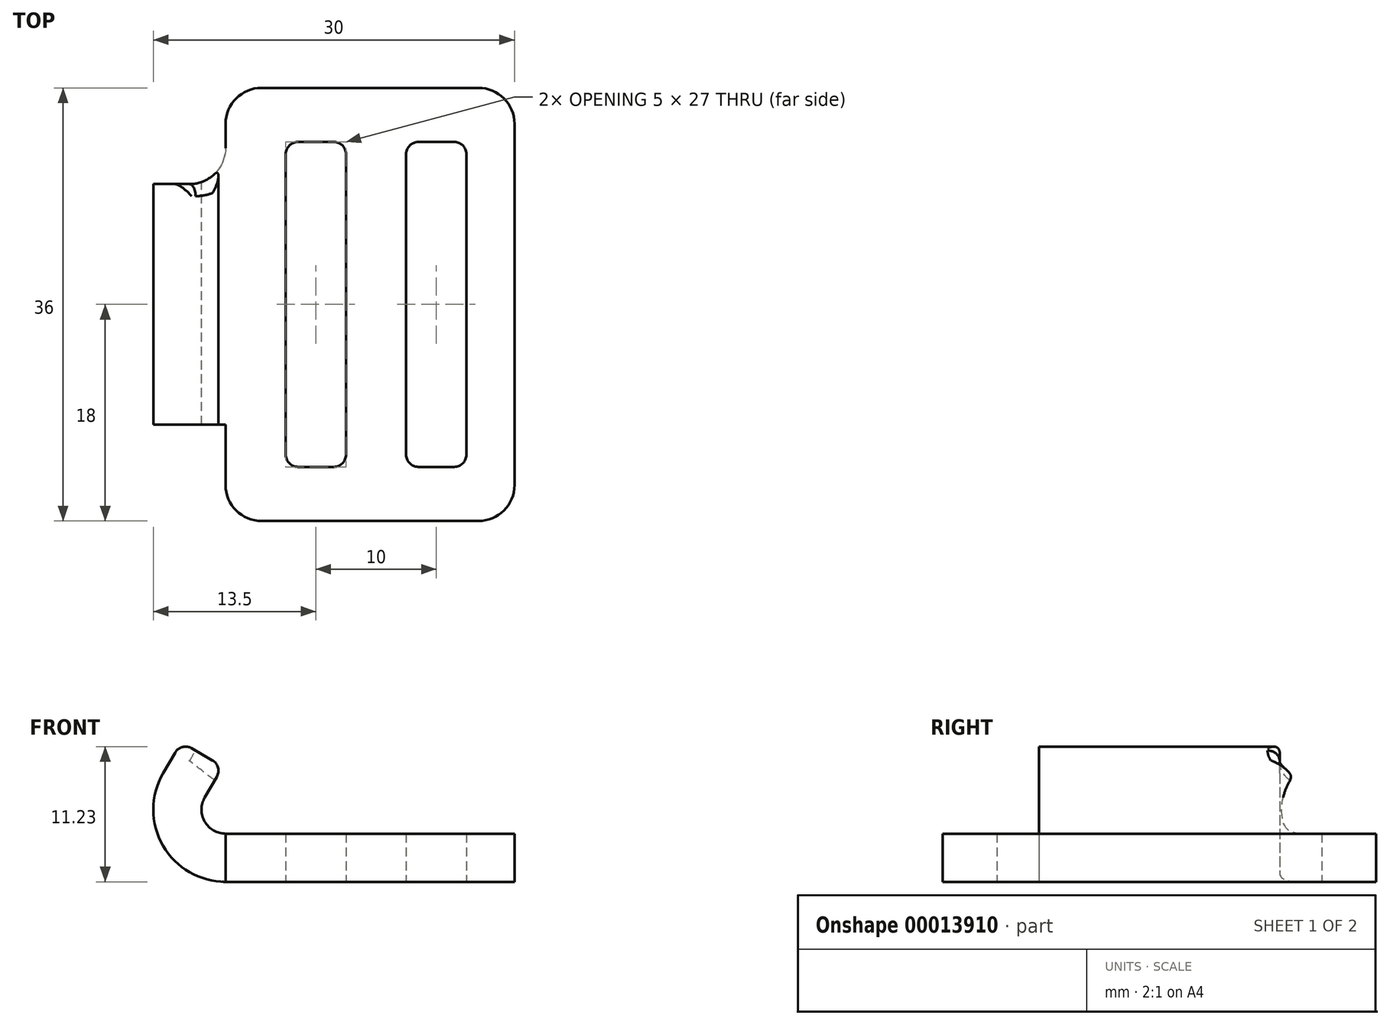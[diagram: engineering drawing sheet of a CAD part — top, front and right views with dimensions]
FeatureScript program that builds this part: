
annotation { "Feature Type Name" : "Feature", "Feature Type Description" : "" }
export const myFeature = defineFeature(function(context is Context, id is Id, definition is map)
    precondition{}
    {
        {
            var Q0;
            Q0=qCreatedBy(makeId("Top.planeOp"),FACE);
            var sketch = newSketch(context, id + "F0", { "sketchPlane" : qUnion([Q0])});
            skLineSegment(sketch, "E0.bottom", {"start": v(13, 18) * mm, "end": v(31, 18) * mm});
            skLineSegment(sketch, "E0.top", {"start": v(13, -18) * mm, "end": v(31, -18) * mm});
            skLineSegment(sketch, "E0.left", {"start": v(10, 15) * mm, "end": v(10, -13.27) * mm});
            skLineSegment(sketch, "E0.right", {"start": v(34, 15) * mm, "end": v(34, -15) * mm});
            skLineSegment(sketch, "E1.trimOffspring", {"start": v(10, -13.27) * mm, "end": v(10, -15) * mm});
            skLineSegment(sketch, "E2.bottom", {"start": v(16, 13.5) * mm, "end": v(19, 13.5) * mm});
            skLineSegment(sketch, "E2.top", {"start": v(16, -13.5) * mm, "end": v(19, -13.5) * mm});
            skLineSegment(sketch, "E2.left", {"start": v(15, 12.5) * mm, "end": v(15, -12.5) * mm});
            skLineSegment(sketch, "E2.right", {"start": v(20, 12.5) * mm, "end": v(20, -12.5) * mm});
            skLineSegment(sketch, "E3.bottom", {"start": v(26, 13.5) * mm, "end": v(29, 13.5) * mm});
            skLineSegment(sketch, "E3.top", {"start": v(26, -13.5) * mm, "end": v(29, -13.5) * mm});
            skLineSegment(sketch, "E3.left", {"start": v(25, 12.5) * mm, "end": v(25, -12.5) * mm});
            skLineSegment(sketch, "E3.right", {"start": v(30, 12.5) * mm, "end": v(30, -12.5) * mm});
            skLineSegment(sketch, "E4", {"start": v(0, 0) * mm, "end": v(34, 0) * mm, "construction": true});
            skPoint(sketch, "E5", {"position": v(25, 0) * mm});
            skPoint(sketch, "E6.visualSharp", {"position": v(10, -18) * mm});
            skArc(sketch, "E6.filletArc", {"start": v(10, -15) * mm, "mid": v(10.88, -17.12) * mm, "end": v(13, -18) * mm});
            skPoint(sketch, "E7.visualSharp", {"position": v(34, -18) * mm});
            skArc(sketch, "E7.filletArc", {"start": v(31, -18) * mm, "mid": v(33.12, -17.12) * mm, "end": v(34, -15) * mm});
            skPoint(sketch, "E8.visualSharp", {"position": v(34, 18) * mm});
            skArc(sketch, "E8.filletArc", {"start": v(34, 15) * mm, "mid": v(33.12, 17.12) * mm, "end": v(31, 18) * mm});
            skPoint(sketch, "E9.visualSharp", {"position": v(10, 18) * mm});
            skArc(sketch, "E9.filletArc", {"start": v(13, 18) * mm, "mid": v(10.88, 17.12) * mm, "end": v(10, 15) * mm});
            skPoint(sketch, "E10.visualSharp", {"position": v(15, 13.5) * mm});
            skArc(sketch, "E10.filletArc", {"start": v(16, 13.5) * mm, "mid": v(15.3, 13.2) * mm, "end": v(15, 12.5) * mm});
            skPoint(sketch, "E11.visualSharp", {"position": v(20, 13.5) * mm});
            skArc(sketch, "E11.filletArc", {"start": v(20, 12.5) * mm, "mid": v(19.7, 13.2) * mm, "end": v(19, 13.5) * mm});
            skPoint(sketch, "E12.visualSharp", {"position": v(25, 13.5) * mm});
            skArc(sketch, "E12.filletArc", {"start": v(26, 13.5) * mm, "mid": v(25.3, 13.2) * mm, "end": v(25, 12.5) * mm});
            skPoint(sketch, "E13.visualSharp", {"position": v(30, 13.5) * mm});
            skArc(sketch, "E13.filletArc", {"start": v(30, 12.5) * mm, "mid": v(29.7, 13.2) * mm, "end": v(29, 13.5) * mm});
            skPoint(sketch, "E14.visualSharp", {"position": v(30, -13.5) * mm});
            skArc(sketch, "E14.filletArc", {"start": v(29, -13.5) * mm, "mid": v(29.7, -13.2) * mm, "end": v(30, -12.5) * mm});
            skPoint(sketch, "E15.visualSharp", {"position": v(25, -13.5) * mm});
            skArc(sketch, "E15.filletArc", {"start": v(25, -12.5) * mm, "mid": v(25.3, -13.2) * mm, "end": v(26, -13.5) * mm});
            skPoint(sketch, "E16.visualSharp", {"position": v(15, -13.5) * mm});
            skArc(sketch, "E16.filletArc", {"start": v(15, -12.5) * mm, "mid": v(15.3, -13.2) * mm, "end": v(16, -13.5) * mm});
            skPoint(sketch, "E17.visualSharp", {"position": v(20, -13.5) * mm});
            skArc(sketch, "E17.filletArc", {"start": v(19, -13.5) * mm, "mid": v(19.7, -13.2) * mm, "end": v(20, -12.5) * mm});
            skSolve(sketch);
        }
        {
            var Q0;
            Q0=qSketchRegion(id+"F0",true);
            extrude(context, id + "F1", {"entities" : qUnion([Q0]), "depth" : 4 * mm});
        }
        {
            var Q0;
            Q0=qCreatedBy(makeId("Front.planeOp"),FACE);
            var sketch = newSketch(context, id + "F2", { "sketchPlane" : qUnion([Q0])});
            skArc(sketch, "E18", {"start": v(4.8, 9) * mm, "mid": v(4.8, 3) * mm, "end": v(10, 0) * mm});
            skLineSegment(sketch, "E19", {"start": v(10, 0) * mm, "end": v(13, 0) * mm, "construction": true});
            skArc(sketch, "E20", {"start": v(8.27, 7) * mm, "mid": v(8.27, 5) * mm, "end": v(10, 4) * mm});
            skLineSegment(sketch, "E21", {"start": v(10, 6) * mm, "end": v(4.8, 9) * mm, "construction": true});
            skLineSegment(sketch, "E22", {"start": v(4.8, 9) * mm, "end": v(6.3, 11.6) * mm});
            skLineSegment(sketch, "E23", {"start": v(6.3, 11.6) * mm, "end": v(9.77, 9.6) * mm});
            skLineSegment(sketch, "E24", {"start": v(9.77, 9.6) * mm, "end": v(8.27, 7) * mm});
            skLineSegment(sketch, "E25", {"start": v(10, 4) * mm, "end": v(10, 0) * mm});
            skSolve(sketch);
        }
        {
            var Q0;
            Q0 = qSketchRegion(id + "F2", true);
            extrude(context, id + "F3", {"entities" : qUnion([Q0]), "operationType" : NewBodyOperationType.ADD, "depth" : 10 * mm, "hasSecondDirection" : true, "secondDirectionOppositeDirection" : true, "secondDirectionDepth" : 10 * mm});
        }
        {
            var Q0;
            Q0=makeQuery(id+"F3.opExtrude","CAP_EDGE",EDGE,{"disambiguationData":[OSD([sQuery(id+"F2.wireOp",EDGE,"E25")])],"isStart":false});
            var Q1;
            Q1=makeQuery(id+"F3.opExtrude","CAP_EDGE",EDGE,{"disambiguationData":[OSD([sQuery(id+"F2.wireOp",EDGE,"E25")])],"isStart":true});
            fillet(context, id + "F4", {"entities" : qUnion([Q0, Q1]), "radius" : 3 * mm, "tangentPropagation" : true, "allowEdgeOverflow" : false});
        }
        {
            var Q0;
            Q0=makeQuery(id+"F4.opFillet","BLEND_EDGE",EDGE,{"blendedFrom":[makeQuery(id+"F3.opExtrude","CAP_EDGE",EDGE,{"disambiguationData":[OSD([sQuery(id+"F2.wireOp",EDGE,"E25")])],"isStart":false}),makeQuery(id+"F3.opExtrude","SWEPT_FACE",FACE,{"disambiguationData":[OSD([sQuery(id+"F2.wireOp",EDGE,"E23")])]})],"blendedInto":[makeQuery(id+"F3.opExtrude","SWEPT_FACE",FACE,{"disambiguationData":[OSD([sQuery(id+"F2.wireOp",EDGE,"E23")])]})]});
            var Q1;
            Q1=makeQuery(id+"F4.opFillet","BLEND_EDGE",EDGE,{"blendedFrom":[makeQuery(id+"F3.opExtrude","CAP_EDGE",EDGE,{"disambiguationData":[OSD([sQuery(id+"F2.wireOp",EDGE,"E25")])],"isStart":true}),makeQuery(id+"F3.opExtrude","SWEPT_FACE",FACE,{"disambiguationData":[OSD([sQuery(id+"F2.wireOp",EDGE,"E23")])]})],"blendedInto":[makeQuery(id+"F3.opExtrude","SWEPT_FACE",FACE,{"disambiguationData":[OSD([sQuery(id+"F2.wireOp",EDGE,"E23")])]})]});
            var Q2;
            Q2=makeQuery(id+"F3.opExtrude","SWEPT_EDGE",EDGE,{"disambiguationData":[OSD([sQuery(id+"F2.wireOp",EDGE,"E22"),sQuery(id+"F2.wireOp",EDGE,"E23")])]});
            var Q3;
            Q3=makeQuery(id+"F3.opExtrude","SWEPT_EDGE",EDGE,{"disambiguationData":[OSD([sQuery(id+"F2.wireOp",EDGE,"E23"),sQuery(id+"F2.wireOp",EDGE,"E24")])]});
            fillet(context, id + "F5", {"entities" : qUnion([Q0, Q1, Q2, Q3]), "radius" : 1 * mm, "tangentPropagation" : true, "allowEdgeOverflow" : false});
        }
    });
